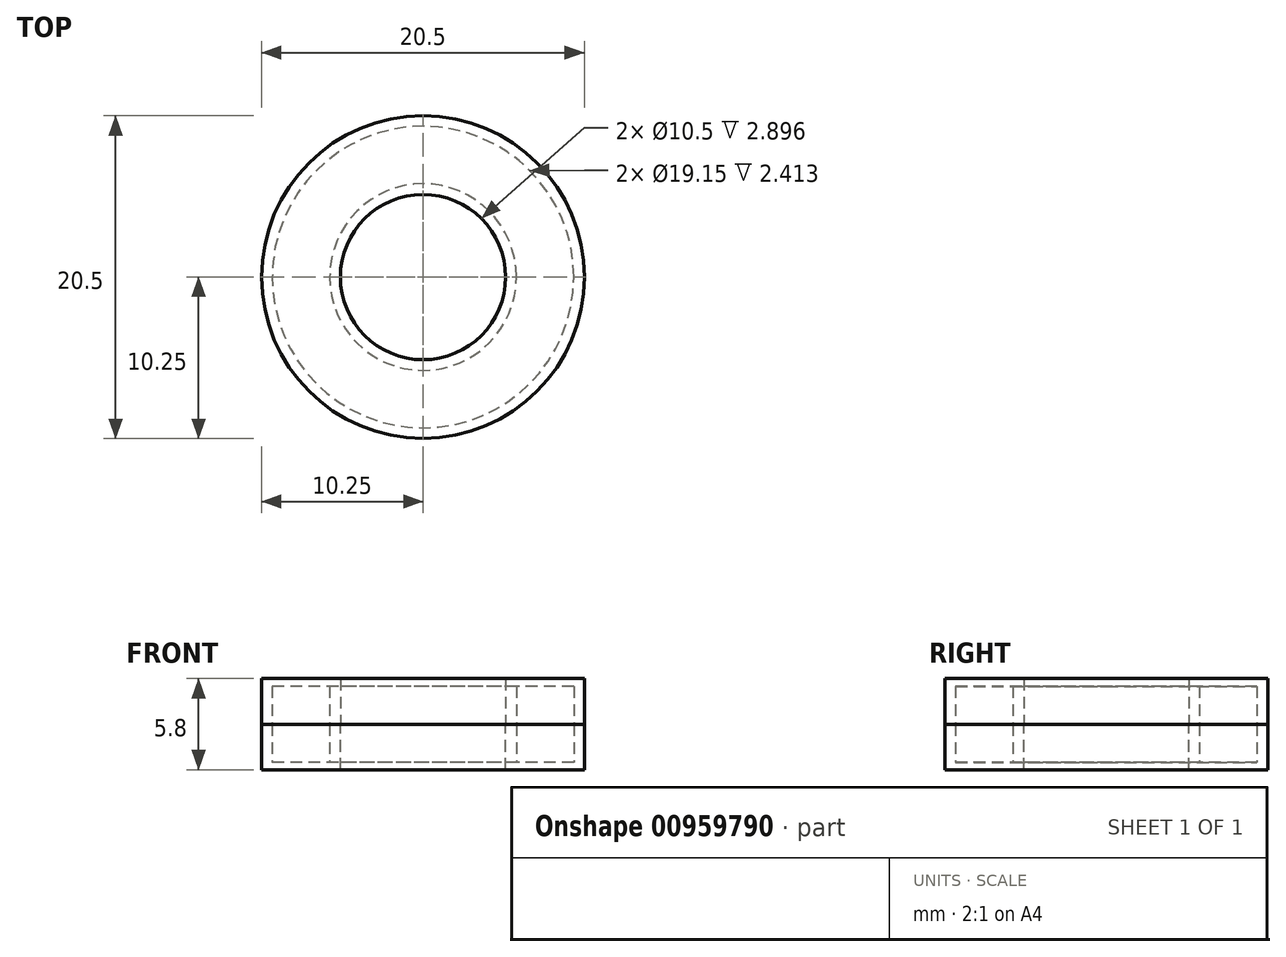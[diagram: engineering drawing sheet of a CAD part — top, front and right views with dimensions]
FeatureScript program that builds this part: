
annotation { "Feature Type Name" : "Feature", "Feature Type Description" : "" }
export const myFeature = defineFeature(function(context is Context, id is Id, definition is map)
    precondition{}
    {
        {
            var Q0;
            Q0=qCreatedBy(makeId("Top.planeOp"),FACE);
            var sketch = newSketch(context, id + "F0", { "sketchPlane" : qUnion([Q0])});
            skCircle(sketch, "E0", {"center": v(0, 0) * mm, "radius": 5.25 * mm});
            skCircle(sketch, "E1", {"center": v(0, 0) * mm, "radius": 10.25 * mm});
            skSolve(sketch);
        }
        {
            var Q0;
            Q0=qCreatedBy(makeId("Top.planeOp"),FACE);
            var sketch = newSketch(context, id + "F1", { "sketchPlane" : qUnion([Q0])});
            skCircle(sketch, "E2", {"center": v(0, 0) * mm, "radius": 5.92 * mm});
            skCircle(sketch, "E3", {"center": v(0, 0) * mm, "radius": 9.57 * mm});
            skSolve(sketch);
        }
        {
            var Q0;
            Q0 = qSketchRegion(id + "F0", true);
            extrude(context, id + "F2", {"entities" : qUnion([Q0]), "depth" : 2.9 * mm, "offsetDistance" : 25.4 * mm});
        }
        {
            var Q0;
            Q0=qCreatedBy(makeId("Top.planeOp"),FACE);
            var sketch = newSketch(context, id + "F3", { "sketchPlane" : qUnion([Q0])});
            skCircle(sketch, "E4", {"center": v(0, 0) * mm, "radius": 5.25 * mm});
            skCircle(sketch, "E5", {"center": v(0, 0) * mm, "radius": 10.25 * mm});
            skSolve(sketch);
        }
        {
            var Q0;
            Q0 = qSketchRegion(id + "F3", true);
            var Q1;
            Q1=sQuery(id+"F3.wireOp",EDGE,"E5");
            var Q2;
            Q2=sQuery(id+"F3.wireOp",EDGE,"E4");
            extrude(context, id + "F4", {"entities" : qUnion([Q0]), "surfaceEntities" : qUnion([Q1, Q2]), "oppositeDirection" : true, "depth" : 2.9 * mm, "offsetDistance" : 25.4 * mm});
        }
        {
            var Q0;
            Q0 = qSketchRegion(id + "F1", true);
            extrude(context, id + "F5", {"entities" : qUnion([Q0]), "operationType" : NewBodyOperationType.REMOVE, "endBound" : BoundingType.SYMMETRIC, "depth" : 4.83 * mm, "offsetDistance" : 25.4 * mm});
        }
    });
